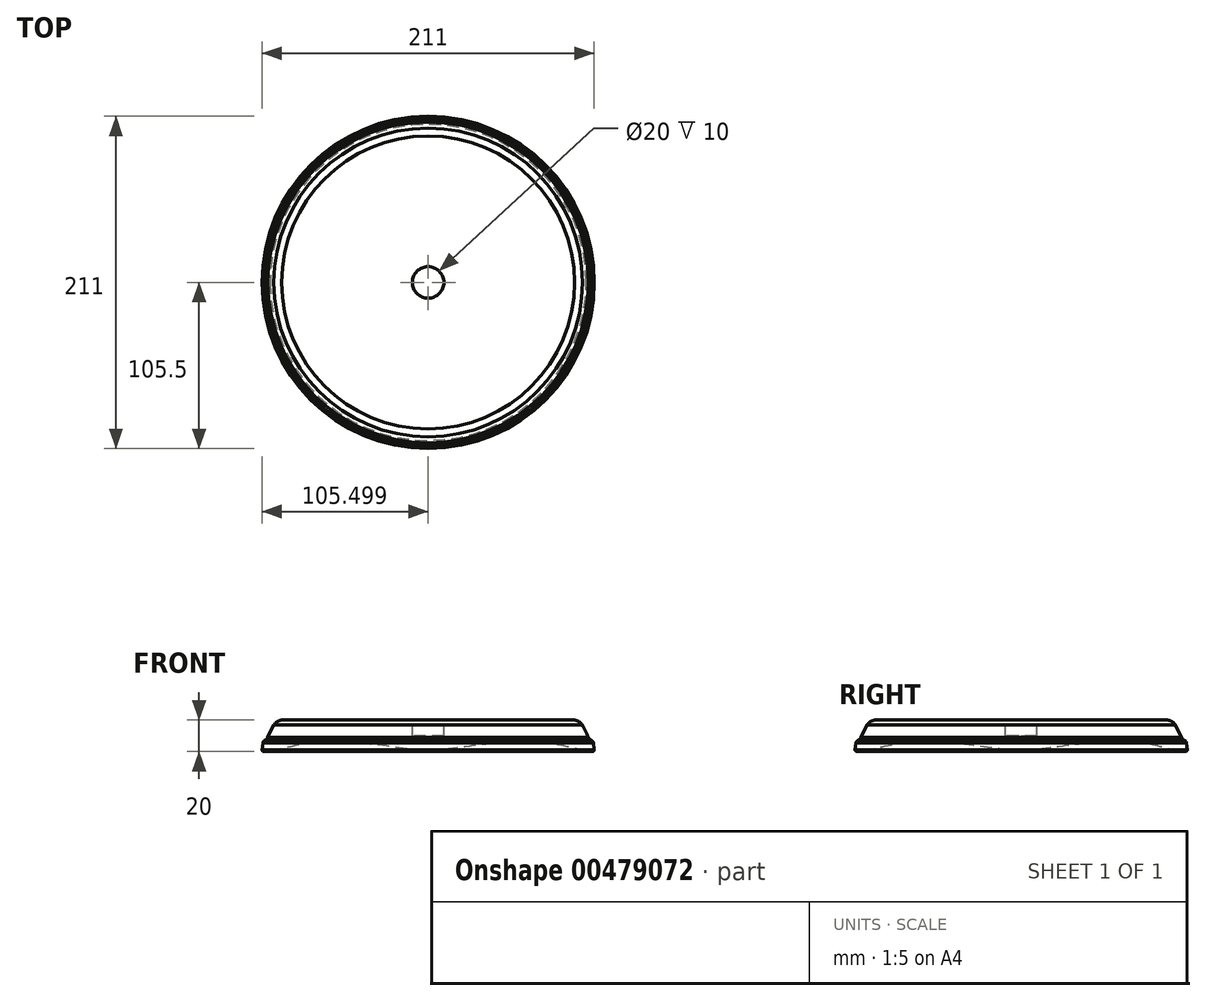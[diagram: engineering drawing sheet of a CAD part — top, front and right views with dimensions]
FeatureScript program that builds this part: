
annotation { "Feature Type Name" : "Feature", "Feature Type Description" : "" }
export const myFeature = defineFeature(function(context is Context, id is Id, definition is map)
    precondition{}
    {
        {
            var Q0;
            Q0=qCreatedBy(makeId("Front.planeOp"),FACE);
            var sketch = newSketch(context, id + "F0", { "sketchPlane" : qUnion([Q0])});
            skLineSegment(sketch, "E0", {"start": v(11.69, 49.56) * mm, "end": v(11.69, -35.56) * mm, "construction": true});
            skLineSegment(sketch, "E1.0", {"start": v(11.69, -15.56) * mm, "end": v(-81.33, -15.56) * mm});
            skLineSegment(sketch, "E2", {"start": v(-88.72, -35.56) * mm, "end": v(-92.7, -35.56) * mm});
            skLineSegment(sketch, "E3", {"start": v(-93.81, -34.38) * mm, "end": v(-93.23, -29.94) * mm});
            skLineSegment(sketch, "E4", {"start": v(-90.17, -26.5) * mm, "end": v(-86.35, -18.78) * mm});
            skArc(sketch, "E5", {"start": v(-81.33, -15.56) * mm, "mid": v(-84.21, -16.59) * mm, "end": v(-86.35, -18.78) * mm});
            skArc(sketch, "E6", {"start": v(-91.99, -28.38) * mm, "mid": v(-90.9, -27.6) * mm, "end": v(-90.17, -26.5) * mm});
            skArc(sketch, "E7", {"start": v(-91.99, -28.38) * mm, "mid": v(-92.78, -29.02) * mm, "end": v(-93.23, -29.94) * mm});
            skArc(sketch, "E8", {"start": v(-93.81, -34.38) * mm, "mid": v(-93.48, -35.18) * mm, "end": v(-92.7, -35.56) * mm});
            skFitSpline(sketch, "E9", {"points": [v(-88.72, -35.56) * mm, v(-54.04, -29.23) * mm, v(11.69, -35.56) * mm], "startDerivative": vector(75.46, 20.47) * mm, "endDerivative": vector(122.9, -18.45) * mm});
            skPoint(sketch, "E10.orphan", {"position": v(-90.9, -27.97) * mm});
            skPoint(sketch, "E11.orphan", {"position": v(-93.07, -28.79) * mm});
            skLineSegment(sketch, "E12", {"start": v(11.69, -15.56) * mm, "end": v(11.69, -35.56) * mm});
            skSolve(sketch);
        }
        {
            var Q0;
            Q0=makeQuery(id+"F0.imprint","IMPRINT",FACE,{"disambiguationData":[TD([[makeQuery(id+"F0.imprint","IMPRINT",EDGE,{"derivedFrom":sQuery(id+"F0.wireOp",EDGE,"E1.0")}),1.0]])]});
            var Q1;
            Q1=sQuery(id+"F0.wireOp",EDGE,"E0");
            revolve(context, id + "F1", {"entities" : qUnion([Q0]), "axis" : qUnion([Q1]), "revolveType" : RevolveType.FULL});
        }
        {
            var Q0;
            Q0=makeQuery(id+"F1.opRevolve","SWEPT_FACE",FACE,{"disambiguationData":[OSD([sQuery(id+"F0.wireOp",EDGE,"E1.0")])]});
            var sketch = newSketch(context, id + "F2", { "sketchPlane" : qUnion([Q0])});
            skCircle(sketch, "E13", {"center": v(11.69, 0) * mm, "radius": 10 * mm});
            skSolve(sketch);
        }
        {
            var Q0;
            Q0=makeQuery(id+"F2.imprint","IMPRINT",FACE,{"disambiguationData":[TD([[makeQuery(id+"F2.imprint","IMPRINT",EDGE,{"derivedFrom":sQuery(id+"F2.wireOp",EDGE,"E13")}),1.0]])]});
            extrude(context, id + "F3", {"entities" : qUnion([Q0]), "operationType" : NewBodyOperationType.REMOVE, "oppositeDirection" : true, "depth" : 10 * mm});
        }
    });
